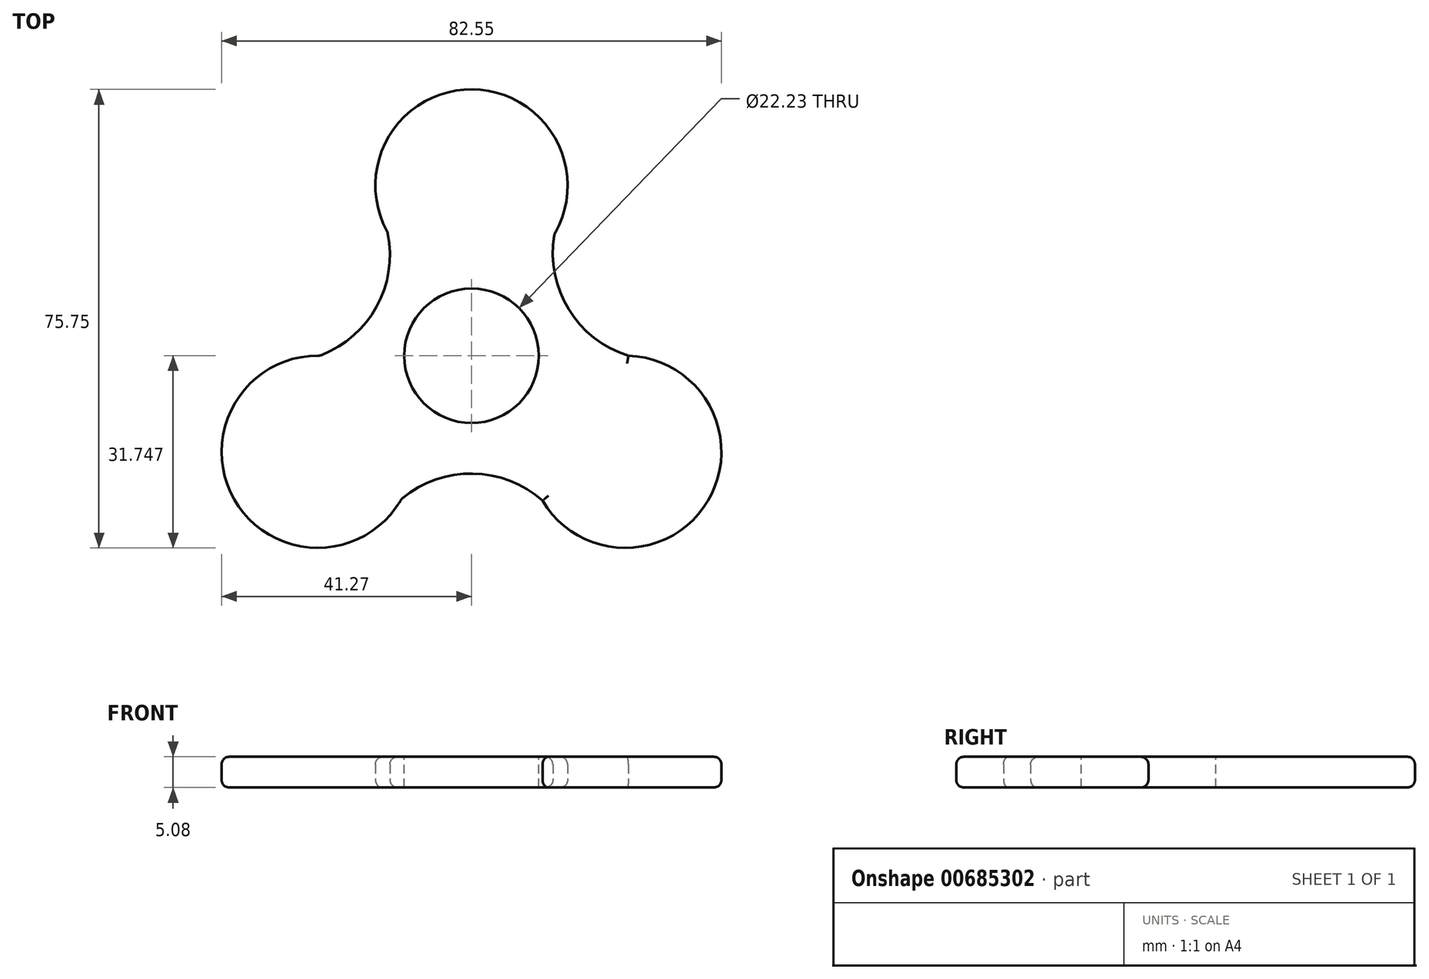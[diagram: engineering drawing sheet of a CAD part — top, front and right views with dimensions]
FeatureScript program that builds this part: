
annotation { "Feature Type Name" : "Feature", "Feature Type Description" : "" }
export const myFeature = defineFeature(function(context is Context, id is Id, definition is map)
    precondition{}
    {
        {
            var Q0;
            Q0=qCreatedBy(makeId("Top.planeOp"),FACE);
            var sketch = newSketch(context, id + "F0", { "sketchPlane" : qUnion([Q0])});
            skArc(sketch, "E0", {"start": v(-25.09, 15.87) * mm, "mid": v(-39.2, -7.84) * mm, "end": v(-11.6, -7.85) * mm});
            skArc(sketch, "E1", {"start": v(13.72, 36) * mm, "mid": v(0.15, 59.87) * mm, "end": v(-13.87, 36.27) * mm});
            skArc(sketch, "E2", {"start": v(-25.09, 15.87) * mm, "mid": v(-15.68, 23.98) * mm, "end": v(-13.87, 36.27) * mm});
            skArc(sketch, "E3", {"start": v(13.72, 36) * mm, "mid": v(16, 23.63) * mm, "end": v(25.91, 15.87) * mm});
            skArc(sketch, "E4", {"start": v(11.73, -8.07) * mm, "mid": v(0.1, -3.6) * mm, "end": v(-11.6, -7.85) * mm});
            skArc(sketch, "E5", {"start": v(11.73, -8.07) * mm, "mid": v(39.06, -8.1) * mm, "end": v(25.91, 15.87) * mm});
            skSolve(sketch);
        }
        {
            var Q0;
            Q0=makeQuery(id+"F0.imprint","IMPRINT",FACE,{"disambiguationData":[TD([[makeQuery(id+"F0.imprint","IMPRINT",EDGE,{"derivedFrom":sQuery(id+"F0.wireOp",EDGE,"E0")}),1.0]])]});
            extrude(context, id + "F1", {"entities" : qUnion([Q0]), "depth" : 5.08 * mm, "offsetDistance" : 25.4 * mm});
        }
        {
            var Q0;
            Q0=makeQuery(id+"F1.opExtrude","CAP_FACE",FACE,{"disambiguationData":[OSD([sQuery(id+"F0.wireOp",EDGE,"E0"),sQuery(id+"F0.wireOp",EDGE,"xiisdPU7-99TD-ywlE-voaA-AwJjjhEJ0wtm"),sQuery(id+"F0.wireOp",EDGE,"E1"),sQuery(id+"F0.wireOp",EDGE,"E2"),sQuery(id+"F0.wireOp",EDGE,"E3"),sQuery(id+"F0.wireOp",EDGE,"E4")])],"isStart":false});
            var sketch = newSketch(context, id + "F2", { "sketchPlane" : qUnion([Q0])});
            skCircle(sketch, "E6", {"center": v(0, 44) * mm, "radius": 11.11 * mm});
            skCircle(sketch, "E7", {"center": v(-25.4, 0) * mm, "radius": 11.11 * mm});
            skCircle(sketch, "E8", {"center": v(25.4, 0) * mm, "radius": 11.11 * mm});
            skCircle(sketch, "E9", {"center": v(0, 15.87) * mm, "radius": 11.11 * mm});
            skSolve(sketch);
        }
        {
            var Q0;
            Q0=makeQuery(id+"F1.opExtrude","SWEPT_FACE",FACE,{"disambiguationData":[OSD([sQuery(id+"F0.wireOp",EDGE,"E1")])]});
            var Q1;
            Q1=makeQuery(id+"F1.opExtrude","SWEPT_FACE",FACE,{"disambiguationData":[OSD([sQuery(id+"F0.wireOp",EDGE,"xiisdPU7-99TD-ywlE-voaA-AwJjjhEJ0wtm")])]});
            var Q2;
            Q2=makeQuery(id+"F1.opExtrude","SWEPT_FACE",FACE,{"disambiguationData":[OSD([sQuery(id+"F0.wireOp",EDGE,"E0")])]});
            var Q3;
            Q3=makeQuery(id+"F1.opExtrude","CAP_EDGE",EDGE,{"disambiguationData":[OSD([sQuery(id+"F0.wireOp",EDGE,"E4")])],"isStart":true});
            var Q4;
            Q4=makeQuery(id+"F1.opExtrude","CAP_EDGE",EDGE,{"disambiguationData":[OSD([sQuery(id+"F0.wireOp",EDGE,"E4")])],"isStart":false});
            var Q5;
            Q5=makeQuery(id+"F1.opExtrude","CAP_EDGE",EDGE,{"disambiguationData":[OSD([sQuery(id+"F0.wireOp",EDGE,"E2")])],"isStart":false});
            var Q6;
            Q6=makeQuery(id+"F1.opExtrude","CAP_EDGE",EDGE,{"disambiguationData":[OSD([sQuery(id+"F0.wireOp",EDGE,"E2")])],"isStart":true});
            var Q7;
            Q7=makeQuery(id+"F1.opExtrude","CAP_EDGE",EDGE,{"disambiguationData":[OSD([sQuery(id+"F0.wireOp",EDGE,"E3")])],"isStart":true});
            var Q8;
            Q8=makeQuery(id+"F1.opExtrude","CAP_EDGE",EDGE,{"disambiguationData":[OSD([sQuery(id+"F0.wireOp",EDGE,"E3")])],"isStart":false});
            var Q9;
            Q9=makeQuery(id+"F1.opExtrude","CAP_EDGE",EDGE,{"disambiguationData":[OSD([sQuery(id+"F0.wireOp",EDGE,"E5")])],"isStart":false});
            var Q10;
            Q10=makeQuery(id+"F1.opExtrude","CAP_EDGE",EDGE,{"disambiguationData":[OSD([sQuery(id+"F0.wireOp",EDGE,"E5")])],"isStart":true});
            fillet(context, id + "F3", {"entities" : qUnion([Q0, Q1, Q2, Q3, Q4, Q5, Q6, Q7, Q8, Q9, Q10]), "radius" : 1.27 * mm, "tangentPropagation" : true, "allowEdgeOverflow" : false});
        }
        {
            var Q0;
            Q0=makeQuery(id+"F2.imprint","IMPRINT",FACE,{"disambiguationData":[TD([[makeQuery(id+"F2.imprint","IMPRINT",EDGE,{"derivedFrom":sQuery(id+"F2.wireOp",EDGE,"E9")}),1.0]])]});
            extrude(context, id + "F4", {"entities" : qUnion([Q0]), "operationType" : NewBodyOperationType.REMOVE, "oppositeDirection" : true, "depth" : 25 * mm, "offsetDistance" : 25 * mm});
        }
    });
